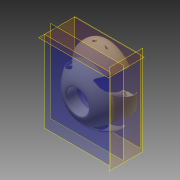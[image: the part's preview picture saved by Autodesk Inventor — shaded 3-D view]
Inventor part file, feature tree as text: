
AUTODESK INVENTOR PART (.ipt)
format: ipt  version: 2014 (Build 180170000, 170)  size: 1,824,768 bytes
history: native  units: mm
features: other x7, fillet x3, extrude x2, sketch x2, mirror x1
ambient origin geometry x8: Origin, YZ Plane, XZ Plane, XY Plane, X Axis, Y Axis, Z Axis, Center Point
bodies: Body1 (feature_tree)
feature tree (15):
  other  "exoskeletal-main.ipt"
  extrude  "押し出し1"  Depth=10.0mm
  mirror  "ミラー1"
  fillet  "フィレット1"  Radius=70.0mm
  other  "作業平面7"
  extrude  "押し出し4"  Depth=0.8mm
  fillet  "フィレット2"  [1 undecoded]
  fillet  "フィレット3"  Radius=10.0mm
  other  "ソリッド1::exoskeletal-main.ipt"
  other  "TaggingFeature1"
  sketch  "スケッチ17"
  other  "作業平面1"
  other  "作業平面6"
  sketch  "スケッチ3"
  other  "ソリッド1"
note: 1 required parameter value undecoded (feature->parameter linkage not recoverable at this tier; creation-order binding heuristic only, values carry confidence <= 0.55)
